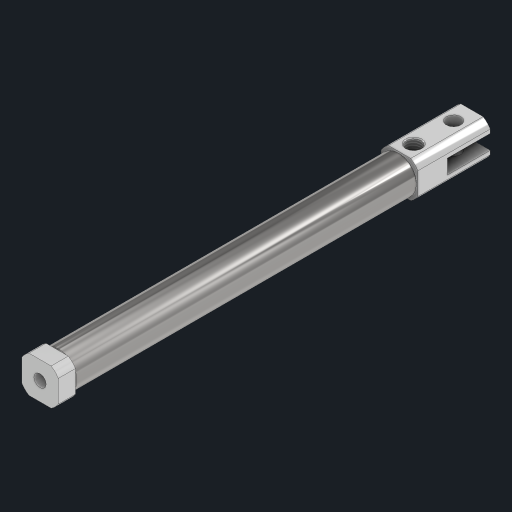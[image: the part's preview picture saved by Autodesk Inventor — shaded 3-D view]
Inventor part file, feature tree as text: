
AUTODESK INVENTOR PART (.ipt)
format: ipt  version: 2023 (Build 270158030, 158C)  size: 185,856 bytes
history: mixed  units: in
note: dims shown in document units (in); Inventor stores cm internally (conversion verified against a paired STEP export)
features: extrude x1, thread x1, sketch x1, other x1, imported_body x1
ambient origin geometry x8: Origin, YZ Plane, XZ Plane, XY Plane, X Axis, Y Axis, Z Axis, Center Point
bodies: Solid1 (imported_parasolid)
feature tree (5):
  extrude  "Extrusion3"  Depth=0.2232in TaperAngle=0.0deg
  thread  "Thread1"  [1 undecoded]
  sketch  "Sketch3"  dims[d4=0.0in d5=0.0in d6=0.2232in d7=0.0in d0=0.0197in d1=0.0344in d2=0.0197in d3=0.0344in]
  other  "D-ClevisPinDetail"
  imported_body  NMx_Import_Brep_tag  [imported B-rep: ~36 faces, bbox_mm=[11.939, 11.938, 140.97]]
note: 1 required parameter value undecoded (feature->parameter linkage not recoverable at this tier; creation-order binding heuristic only, values carry confidence <= 0.55)
